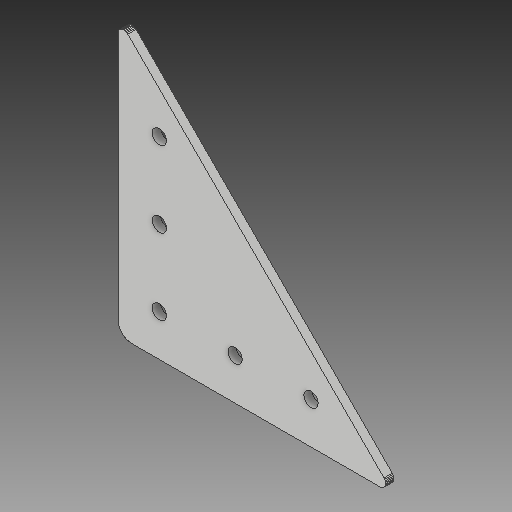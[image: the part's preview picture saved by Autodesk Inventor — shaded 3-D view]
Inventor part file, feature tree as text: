
AUTODESK INVENTOR PART (.ipt)
format: ipt  version: 2018 (Build 220112000, 112)  size: 349,696 bytes
history: native  units: mm
features: sketch x2, extrude x1, hole x1, projected_geometry x1
ambient origin geometry x8: Origin, YZ Plane, XZ Plane, XY Plane, X Axis, Y Axis, Z Axis, Center Point
bodies: Solid1 (feature_tree)
feature tree (5):
  extrude  "Extrusion1"  [1 undecoded]
  hole  "Hole1"  [1 undecoded]
  sketch  "Sketch1"  dims[d0=3.0mm d1=0.0mm]
  sketch  "Sketch2"  dims[d2=5.2mm d3=6.0mm d4=4.0mm d5=2.0mm d6=90.0deg d7=8.0mm d8=20.594885mm]
  projected_geometry  "Projected Loop1"
note: 2 required parameter values undecoded (feature->parameter linkage not recoverable at this tier; creation-order binding heuristic only, values carry confidence <= 0.55)
